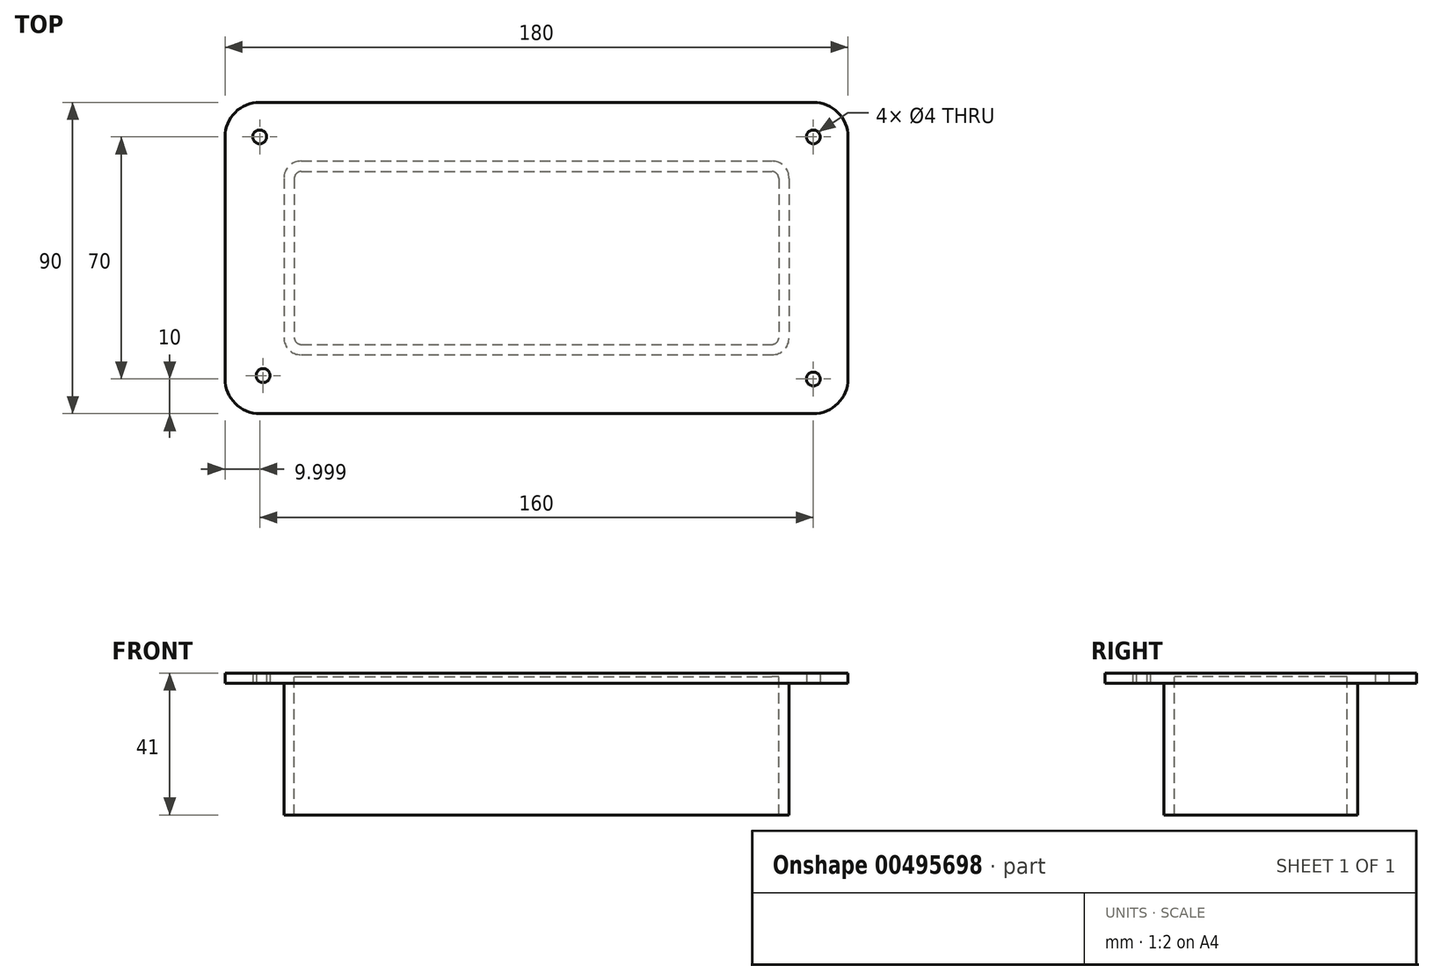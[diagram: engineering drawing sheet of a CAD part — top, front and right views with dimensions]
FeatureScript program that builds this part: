
annotation { "Feature Type Name" : "Feature", "Feature Type Description" : "" }
export const myFeature = defineFeature(function(context is Context, id is Id, definition is map)
    precondition{}
    {
        {
            var Q0;
            Q0=qCreatedBy(makeId("Top.planeOp"),FACE);
            var sketch = newSketch(context, id + "F0", { "sketchPlane" : qUnion([Q0])});
            skLineSegment(sketch, "E0.bottom", {"start": v(-112.53, 11.67) * mm, "end": v(23.47, 11.67) * mm});
            skLineSegment(sketch, "E0.top", {"start": v(-112.53, -38.33) * mm, "end": v(23.47, -38.33) * mm});
            skLineSegment(sketch, "E0.left", {"start": v(-114.53, 9.67) * mm, "end": v(-114.53, -36.33) * mm});
            skLineSegment(sketch, "E0.right", {"start": v(25.47, 9.67) * mm, "end": v(25.47, -36.33) * mm});
            skLineSegment(sketch, "E1.0", {"start": v(-134.53, 21.67) * mm, "end": v(-134.53, -48.33) * mm});
            skLineSegment(sketch, "E1.1", {"start": v(-124.53, 31.67) * mm, "end": v(35.47, 31.67) * mm});
            skLineSegment(sketch, "E1.2", {"start": v(45.47, 21.67) * mm, "end": v(45.47, -48.33) * mm});
            skLineSegment(sketch, "E1.3", {"start": v(-124.53, -58.33) * mm, "end": v(35.47, -58.33) * mm});
            skPoint(sketch, "E2.visualSharp", {"position": v(-134.53, -58.33) * mm});
            skArc(sketch, "E2.filletArc", {"start": v(-134.53, -48.33) * mm, "mid": v(-131.6, -55.4) * mm, "end": v(-124.53, -58.33) * mm});
            skPoint(sketch, "E3.visualSharp", {"position": v(-134.53, 31.67) * mm});
            skArc(sketch, "E3.filletArc", {"start": v(-124.53, 31.67) * mm, "mid": v(-131.6, 28.74) * mm, "end": v(-134.53, 21.67) * mm});
            skPoint(sketch, "E4.visualSharp", {"position": v(45.47, 31.67) * mm});
            skArc(sketch, "E4.filletArc", {"start": v(45.47, 21.67) * mm, "mid": v(42.54, 28.74) * mm, "end": v(35.47, 31.67) * mm});
            skPoint(sketch, "E5.visualSharp", {"position": v(45.47, -58.33) * mm});
            skArc(sketch, "E5.filletArc", {"start": v(35.47, -58.33) * mm, "mid": v(42.54, -55.4) * mm, "end": v(45.47, -48.33) * mm});
            skPoint(sketch, "E6.visualSharp", {"position": v(-114.53, 11.67) * mm});
            skArc(sketch, "E6.filletArc", {"start": v(-112.53, 11.67) * mm, "mid": v(-113.94, 11.08) * mm, "end": v(-114.53, 9.67) * mm});
            skPoint(sketch, "E7.visualSharp", {"position": v(-114.53, -38.33) * mm});
            skArc(sketch, "E7.filletArc", {"start": v(-114.53, -36.33) * mm, "mid": v(-113.94, -37.74) * mm, "end": v(-112.53, -38.33) * mm});
            skPoint(sketch, "E8.visualSharp", {"position": v(25.47, -38.33) * mm});
            skArc(sketch, "E8.filletArc", {"start": v(23.47, -38.33) * mm, "mid": v(24.88, -37.74) * mm, "end": v(25.47, -36.33) * mm});
            skPoint(sketch, "E9.visualSharp", {"position": v(25.47, 11.67) * mm});
            skArc(sketch, "E9.filletArc", {"start": v(25.47, 9.67) * mm, "mid": v(24.88, 11.08) * mm, "end": v(23.47, 11.67) * mm});
            skCircle(sketch, "E10", {"center": v(-124.53, 21.67) * mm, "radius": 2 * mm});
            skCircle(sketch, "E11", {"center": v(-123.53, -47.33) * mm, "radius": 2 * mm});
            skCircle(sketch, "E12", {"center": v(35.47, -48.33) * mm, "radius": 2 * mm});
            skCircle(sketch, "E13", {"center": v(35.47, 21.67) * mm, "radius": 2 * mm});
            skArc(sketch, "E14.0", {"start": v(-112.53, 14.67) * mm, "mid": v(-116.07, 13.2) * mm, "end": v(-117.53, 9.67) * mm});
            skLineSegment(sketch, "E14.1", {"start": v(-112.53, 14.67) * mm, "end": v(23.47, 14.67) * mm});
            skLineSegment(sketch, "E14.2", {"start": v(-117.53, 9.67) * mm, "end": v(-117.53, -36.33) * mm});
            skArc(sketch, "E14.3", {"start": v(28.47, 9.67) * mm, "mid": v(27, 13.2) * mm, "end": v(23.47, 14.67) * mm});
            skArc(sketch, "E14.4", {"start": v(-117.53, -36.33) * mm, "mid": v(-116.07, -39.87) * mm, "end": v(-112.53, -41.33) * mm});
            skLineSegment(sketch, "E14.5", {"start": v(-112.53, -41.33) * mm, "end": v(23.47, -41.33) * mm});
            skArc(sketch, "E14.6", {"start": v(23.47, -41.33) * mm, "mid": v(27, -39.87) * mm, "end": v(28.47, -36.33) * mm});
            skLineSegment(sketch, "E14.7", {"start": v(28.47, 9.67) * mm, "end": v(28.47, -36.33) * mm});
            skSolve(sketch);
        }
        {
            var Q0;
            Q0=makeQuery(id+"F0.imprint","IMPRINT",FACE,{"disambiguationData":[TD([[makeQuery(id+"F0.imprint","IMPRINT",EDGE,{"derivedFrom":sQuery(id+"F0.wireOp",EDGE,"E0.bottom")}),1.0]])]});
            extrude(context, id + "F1", {"entities" : qUnion([Q0]), "oppositeDirection" : true, "depth" : 40 * mm});
        }
        {
            var Q0;
            Q0=makeQuery(id+"F0.imprint","IMPRINT",FACE,{"disambiguationData":[TD([[makeQuery(id+"F0.imprint","IMPRINT",EDGE,{"derivedFrom":sQuery(id+"F0.wireOp",EDGE,"E1.0")}),1.0]])]});
            extrude(context, id + "F2", {"entities" : qUnion([Q0]), "depth" : 1 * mm});
        }
        {
            var Q0;
            Q0=makeQuery(id+"F0.imprint","IMPRINT",FACE,{"disambiguationData":[TD([[makeQuery(id+"F0.imprint","IMPRINT",EDGE,{"derivedFrom":sQuery(id+"F0.wireOp",EDGE,"E1.0")}),1.0]])]});
            extrude(context, id + "F3", {"entities" : qUnion([Q0]), "operationType" : NewBodyOperationType.ADD, "oppositeDirection" : true, "depth" : 2 * mm});
        }
        {
            var Q0;
            Q0=makeQuery(id+"F0.imprint","IMPRINT",FACE,{"disambiguationData":[TD([[makeQuery(id+"F0.imprint","IMPRINT",EDGE,{"derivedFrom":sQuery(id+"F0.wireOp",EDGE,"E0.bottom")}),-1.0]])]});
            var Q1;
            Q1=makeQuery(id+"F0.imprint","IMPRINT",FACE,{"disambiguationData":[TD([[makeQuery(id+"F0.imprint","IMPRINT",EDGE,{"derivedFrom":sQuery(id+"F0.wireOp",EDGE,"E0.bottom")}),1.0]])]});
            extrude(context, id + "F4", {"entities" : qUnion([Q0, Q1]), "operationType" : NewBodyOperationType.ADD, "depth" : 1 * mm});
        }
    });
